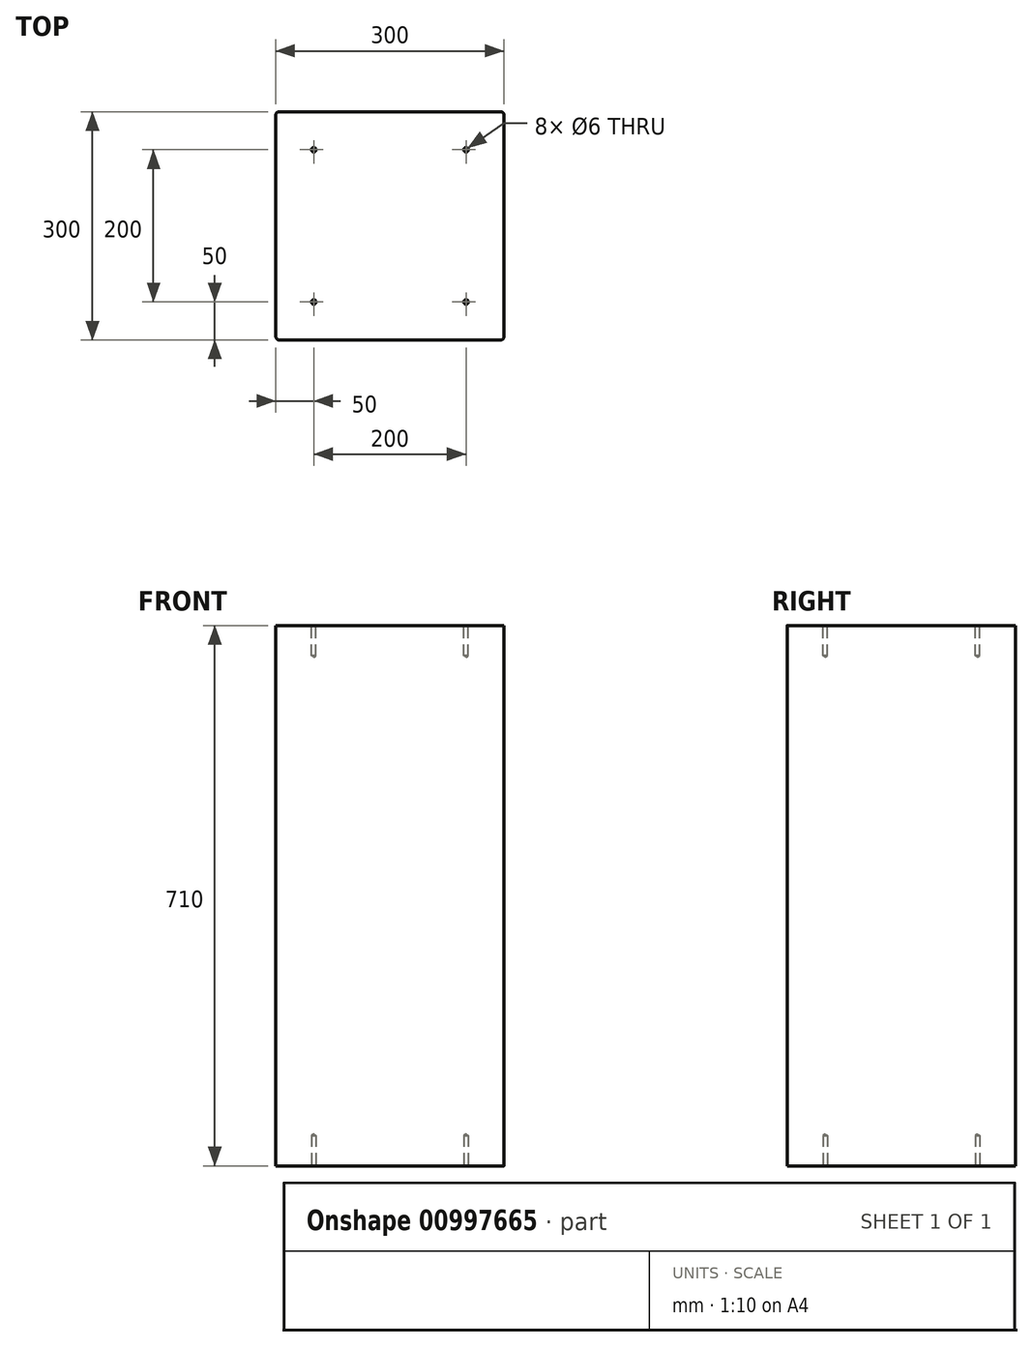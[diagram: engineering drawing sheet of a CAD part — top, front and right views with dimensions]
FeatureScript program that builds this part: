
annotation { "Feature Type Name" : "Feature", "Feature Type Description" : "" }
export const myFeature = defineFeature(function(context is Context, id is Id, definition is map)
    precondition{}
    {
        {
            var Q0;
            Q0=qCreatedBy(makeId("Top.planeOp"),FACE);
            var sketch = newSketch(context, id + "F0", { "sketchPlane" : qUnion([Q0])});
            skLineSegment(sketch, "E0.bottom", {"start": v(0, 0) * mm, "end": v(300, 0) * mm});
            skLineSegment(sketch, "E0.top", {"start": v(0, -300) * mm, "end": v(300, -300) * mm});
            skLineSegment(sketch, "E0.left", {"start": v(0, 0) * mm, "end": v(0, -300) * mm});
            skLineSegment(sketch, "E0.right", {"start": v(300, 0) * mm, "end": v(300, -300) * mm});
            skSolve(sketch);
        }
        {
            var Q0;
            Q0=makeQuery(id+"F0.imprint","IMPRINT",FACE,{"disambiguationData":[TD([[makeQuery(id+"F0.imprint","IMPRINT",EDGE,{"derivedFrom":sQuery(id+"F0.wireOp",EDGE,"E0.bottom")}),-1.0]])]});
            extrude(context, id + "F1", {"entities" : qUnion([Q0]), "depth" : 710 * mm, "offsetDistance" : 25 * mm});
        }
        {
            var Q0;
            Q0=makeQuery(id+"F1.opExtrude","SWEPT_EDGE",EDGE,{"disambiguationData":[OSD([sQuery(id+"F0.wireOp",EDGE,"E0.top"),sQuery(id+"F0.wireOp",EDGE,"E0.left")])]});
            var Q1;
            Q1=makeQuery(id+"F1.opExtrude","SWEPT_EDGE",EDGE,{"disambiguationData":[OSD([sQuery(id+"F0.wireOp",EDGE,"E0.bottom"),sQuery(id+"F0.wireOp",EDGE,"E0.left")])]});
            var Q2;
            Q2=makeQuery(id+"F1.opExtrude","SWEPT_EDGE",EDGE,{"disambiguationData":[OSD([sQuery(id+"F0.wireOp",EDGE,"E0.bottom"),sQuery(id+"F0.wireOp",EDGE,"E0.right")])]});
            var Q3;
            Q3=makeQuery(id+"F1.opExtrude","SWEPT_EDGE",EDGE,{"disambiguationData":[OSD([sQuery(id+"F0.wireOp",EDGE,"E0.top"),sQuery(id+"F0.wireOp",EDGE,"E0.right")])]});
            fillet(context, id + "F2", {"entities" : qUnion([Q0, Q1, Q2, Q3]), "tangentPropagation" : true, "radius" : 5 * mm, "defaultsChanged" : false, "vertexSettings" : [], "allowEdgeOverflow" : false});
        }
        {
            var Q0;
            Q0=makeQuery(id+"F1.opExtrude","CAP_FACE",FACE,{"disambiguationData":[OSD([sQuery(id+"F0.wireOp",EDGE,"E0.bottom"),sQuery(id+"F0.wireOp",EDGE,"E0.top"),sQuery(id+"F0.wireOp",EDGE,"E0.left"),sQuery(id+"F0.wireOp",EDGE,"E0.right")])],"isStart":false});
            var sketch = newSketch(context, id + "F3", { "sketchPlane" : qUnion([Q0])});
            skPoint(sketch, "E1", {"position": v(250, -250) * mm});
            skPoint(sketch, "E2.0.1.0", {"position": v(250, -50) * mm});
            skPoint(sketch, "E2.1.0.0", {"position": v(50, -250) * mm});
            skPoint(sketch, "E2.1.1.0", {"position": v(50, -50) * mm});
            skLineSegment(sketch, "E2.direction1", {"start": v(250, -250) * mm, "end": v(50, -250) * mm, "construction": true});
            skLineSegment(sketch, "E2.direction2", {"start": v(250, -250) * mm, "end": v(250, -50) * mm, "construction": true});
            skSolve(sketch);
        }
        {
            var Q0;
            Q0=sQuery(id+"F3.wireOp",VERTEX,"E1");
            var Q1;
            Q1=sQuery(id+"F3.wireOp",VERTEX,"E2.0.1.0");
            var Q2;
            Q2=sQuery(id+"F3.wireOp",VERTEX,"E2.1.0.0");
            var Q3;
            Q3=sQuery(id+"F3.wireOp",VERTEX,"E2.1.1.0");
            var Q4;
            Q4=makeQuery(id+"F1.opExtrude","SWEPT_BODY",BODY,{"disambiguationData":[OSD([sQuery(id+"F0.wireOp",EDGE,"E0.bottom"),sQuery(id+"F0.wireOp",EDGE,"E0.top"),sQuery(id+"F0.wireOp",EDGE,"E0.left"),sQuery(id+"F0.wireOp",EDGE,"E0.right")])]});
            hole(context, id + "F4", {"style" : HoleStyle.SIMPLE, "endStyle" : HoleEndStyle.BLIND, "holeDiameter" : 6 * mm, "majorDiameter" : 5 * mm, "holeDepth" : 40 * mm, "isTappedThrough" : true, "tappedDepth" : 12 * mm, "tapClearance" : 3, "locations" : qUnion([Q0, Q1, Q2, Q3]), "scope" : qUnion([Q4])});
        }
        {
            var Q0;
            Q0=makeQuery(id+"F1.opExtrude","CAP_FACE",FACE,{"disambiguationData":[OSD([sQuery(id+"F0.wireOp",EDGE,"E0.bottom"),sQuery(id+"F0.wireOp",EDGE,"E0.top"),sQuery(id+"F0.wireOp",EDGE,"E0.left"),sQuery(id+"F0.wireOp",EDGE,"E0.right")])],"isStart":true});
            var sketch = newSketch(context, id + "F5", { "sketchPlane" : qUnion([Q0])});
            skLineSegment(sketch, "E3.bottom", {"start": v(50, 250) * mm, "end": v(250, 250) * mm, "construction": true});
            skLineSegment(sketch, "E3.top", {"start": v(50, 50) * mm, "end": v(250, 50) * mm, "construction": true});
            skLineSegment(sketch, "E3.left", {"start": v(50, 250) * mm, "end": v(50, 50) * mm, "construction": true});
            skLineSegment(sketch, "E3.right", {"start": v(250, 250) * mm, "end": v(250, 50) * mm, "construction": true});
            skSolve(sketch);
        }
        {
            var Q0;
            Q0=sQuery(id+"F5.wireOp",VERTEX,"E3.bottom.start");
            var Q1;
            Q1=sQuery(id+"F5.wireOp",VERTEX,"E3.top.start");
            var Q2;
            Q2=sQuery(id+"F5.wireOp",VERTEX,"E3.top.end");
            var Q3;
            Q3=sQuery(id+"F5.wireOp",VERTEX,"E3.bottom.end");
            var Q4;
            Q4=makeQuery(id+"F1.opExtrude","SWEPT_BODY",BODY,{"disambiguationData":[OSD([sQuery(id+"F0.wireOp",EDGE,"E0.bottom"),sQuery(id+"F0.wireOp",EDGE,"E0.top"),sQuery(id+"F0.wireOp",EDGE,"E0.left"),sQuery(id+"F0.wireOp",EDGE,"E0.right")])]});
            hole(context, id + "F6", {"style" : HoleStyle.SIMPLE, "endStyle" : HoleEndStyle.BLIND, "holeDiameter" : 6 * mm, "majorDiameter" : 5 * mm, "holeDepth" : 40 * mm, "isTappedThrough" : true, "tappedDepth" : 12 * mm, "tapClearance" : 3, "locations" : qUnion([Q0, Q1, Q2, Q3]), "scope" : qUnion([Q4])});
        }
    });
